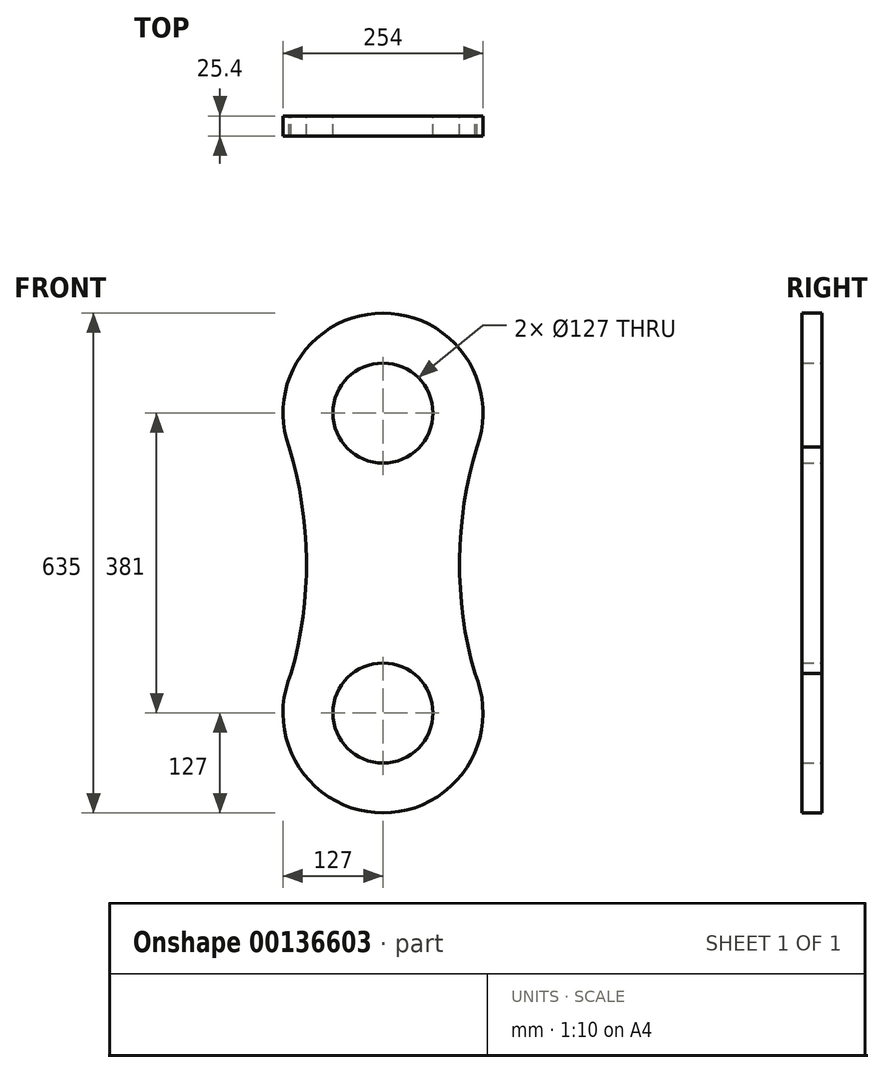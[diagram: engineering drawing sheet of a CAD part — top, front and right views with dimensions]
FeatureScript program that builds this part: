
annotation { "Feature Type Name" : "Feature", "Feature Type Description" : "" }
export const myFeature = defineFeature(function(context is Context, id is Id, definition is map)
    precondition{}
    {
        {
            var Q0;
            Q0=qCreatedBy(makeId("Front.planeOp"),FACE);
            var sketch = newSketch(context, id + "F0", { "sketchPlane" : qUnion([Q0])});
            skArc(sketch, "E0", {"start": v(119.49, 147.47) * mm, "mid": v(0, 317.5) * mm, "end": v(-119.49, 147.47) * mm});
            skArc(sketch, "E1", {"start": v(-116.6, -140.18) * mm, "mid": v(0, -317.5) * mm, "end": v(116.6, -140.18) * mm});
            skCircle(sketch, "E2", {"center": v(0, 190.5) * mm, "radius": 63.5 * mm});
            skCircle(sketch, "E3", {"center": v(0, -190.5) * mm, "radius": 63.5 * mm});
            skArc(sketch, "E4", {"start": v(-116.6, -140.18) * mm, "mid": v(-97.33, 8.79) * mm, "end": v(-122.47, 156.87) * mm});
            skArc(sketch, "E5.MirrorCS", {"start": v(116.6, -140.18) * mm, "mid": v(97.33, 8.79) * mm, "end": v(122.47, 156.87) * mm});
            skSolve(sketch);
        }
        {
            var Q0;
            Q0 = qSketchRegion(id + "F0", true);
            extrude(context, id + "F1", {"entities" : qUnion([Q0]), "depth" : 25.4 * mm});
        }
    });
